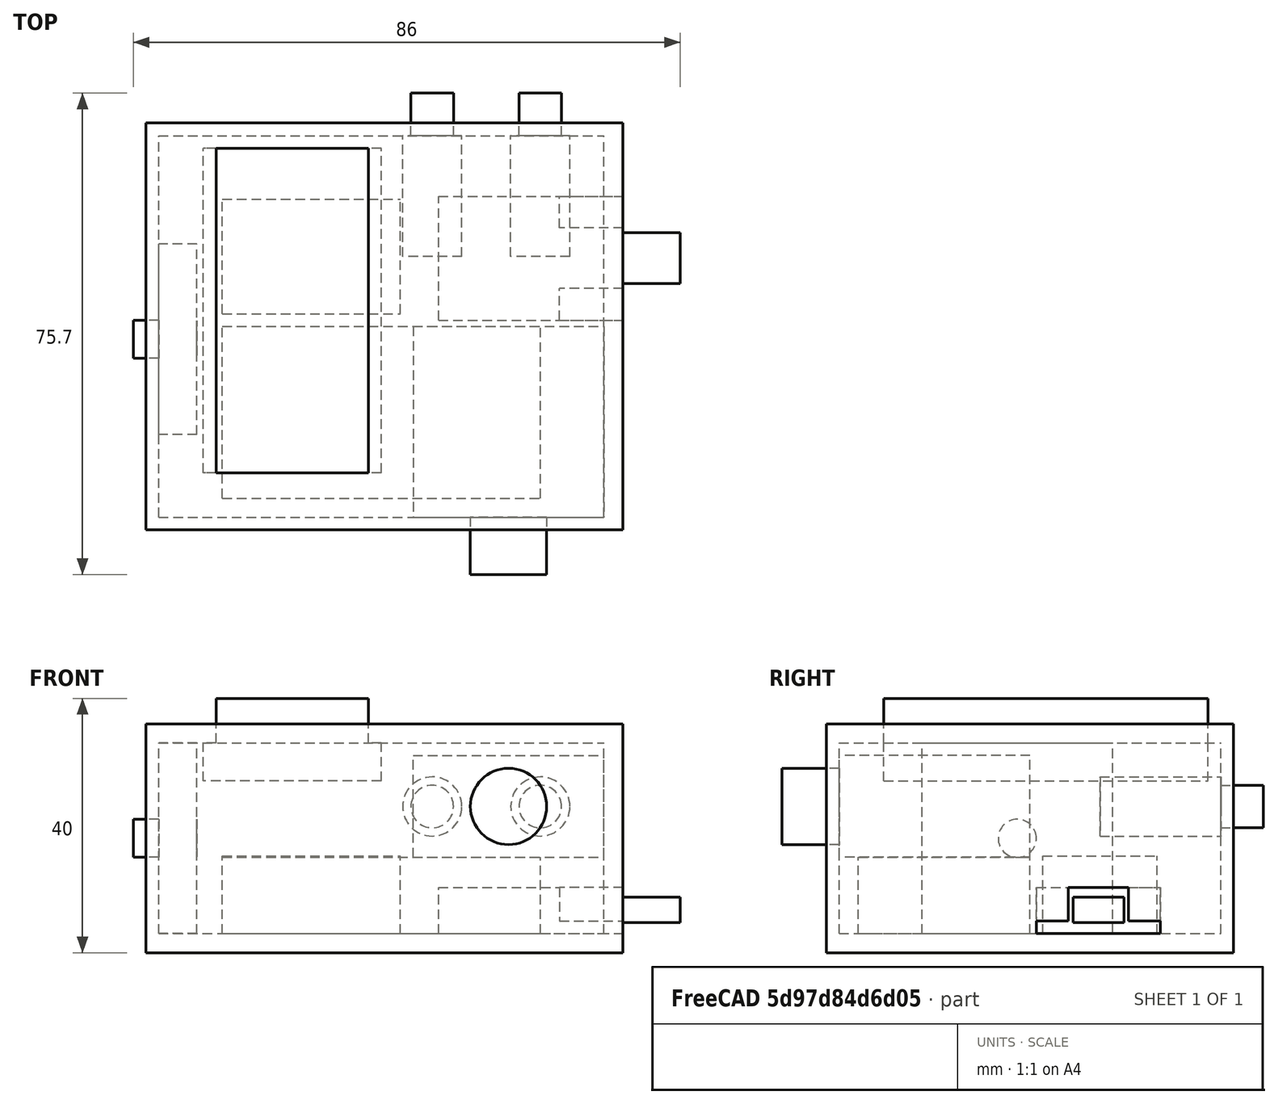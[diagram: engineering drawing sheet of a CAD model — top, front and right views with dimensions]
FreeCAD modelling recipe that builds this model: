
FCSTD DOCUMENT  (FreeCAD 0.19R)
Label: RoundTimer-precuts
License: All rights reserved
LicenseURL: http://en.wikipedia.org/wiki/All_rights_reserved
objects: Part::Box×12, Part::Cylinder×6, Part::MultiFuse×4, Part::Fuse×2, Part::Cut×2
note: 26 computed .brp shape members not serialized (recipe doc carries the construction recipe); baked Part::Feature solids carry a one-line shape summary decoded from their .brp

FEATURE [Part::Box] Box  label="Cube"
  AttacherType = Attacher::AttachEngine3D
  Height = 30
  Length = 30
  Width = 16
FEATURE [Part::Cylinder] Cylinder
  Angle = 360
  AttacherType = Attacher::AttachEngine3D
  Height = 9
  Placement = pos=(15,8,30) rot=(0,0,1;0rad)
  Radius = 6
FEATURE [Part::Fuse] Fusion  label="Awesome switch"
  Base = -> Box
  Placement = pos=(0,17,12) rot=(1,0,0;1.5708rad)
  Tool = -> Cylinder
FEATURE [Part::Box] Box001  label="Cube001"
  AttacherType = Attacher::AttachEngine3D
  Height = 6
  Length = 51
  Width = 28
FEATURE [Part::Box] Box002  label="Cube002"
  AttacherType = Attacher::AttachEngine3D
  Height = 7
  Length = 51
  Placement = pos=(0,2,6) rot=(0,0,1;0rad)
  Width = 24
FEATURE [Part::MultiFuse] Fusion001  label="LCD Display"
  Placement = pos=(-5,-6,24) rot=(0,0,1;1.5708rad)
  Shapes = -> [Box001,Box002]
FEATURE [Part::Box] Box003  label="Lipo Battery"
  AttacherType = Attacher::AttachEngine3D
  Height = 12
  Length = 50
  Placement = pos=(-30,-10,0) rot=(0,0,1;0rad)
  Width = 27
FEATURE [Part::Cylinder] Cylinder001
  Angle = 360
  AttacherType = Attacher::AttachEngine3D
  Height = 19
  Radius = 4.65
FEATURE [Part::Cylinder] Cylinder002
  Angle = 360
  AttacherType = Attacher::AttachEngine3D
  Height = 6.7
  Placement = pos=(0,0,19) rot=(0,0,1;0rad)
  Radius = 3.35
FEATURE [Part::MultiFuse] Fusion002  label="Push Button mode/reset"
  Placement = pos=(20,28,20) rot=(1,0,0;-1.5708rad)
  Shapes = -> [Cylinder001,Cylinder002]
FEATURE [Part::Cylinder] Cylinder003
  Angle = 360
  AttacherType = Attacher::AttachEngine3D
  Height = 19
  Radius = 4.65
FEATURE [Part::Cylinder] Cylinder004
  Angle = 360
  AttacherType = Attacher::AttachEngine3D
  Height = 6.7
  Placement = pos=(0,0,19) rot=(0,0,1;0rad)
  Radius = 3.35
FEATURE [Part::MultiFuse] Fusion003  label="Push Button start/stop"
  Placement = pos=(3,28,20) rot=(1,0,0;-1.5708rad)
  Shapes = -> [Cylinder003,Cylinder004]
FEATURE [Part::Box] Box004  label="Cube003"
  AttacherType = Attacher::AttachEngine3D
  Height = 7.25
  Length = 29
  Width = 19.5
FEATURE [Part::Box] Box005  label="Cube004"
  AttacherType = Attacher::AttachEngine3D
  Height = 4
  Length = 10
  Placement = pos=(28,5.75,1.75) rot=(0,0,1;0rad)
  Width = 8
FEATURE [Part::Box] Box006  label="Cube005"
  AttacherType = Attacher::AttachEngine3D
  Height = 10
  Length = 10
  Placement = pos=(19,-5,2) rot=(0,0,1;0rad)
  Width = 10
FEATURE [Part::MultiFuse] Fusion004
  Shapes = -> [Box004,Box005]
FEATURE [Part::Cut] Cut
  Base = -> Fusion004
  Tool = -> Box006
FEATURE [Part::Box] Box007  label="Cube006"
  AttacherType = Attacher::AttachEngine3D
  Height = 10
  Length = 10
  Placement = pos=(19,14.5,2) rot=(0,0,1;0rad)
  Width = 10
FEATURE [Part::Cut] Cut001  label="USB Battery Charger"
  Base = -> Cut
  Placement = pos=(4,18,0) rot=(0,0,1;0rad)
  Tool = -> Box007
FEATURE [Part::Box] Box008  label="Piezo Driver"
  AttacherType = Attacher::AttachEngine3D
  Height = 12.2
  Length = 28
  Placement = pos=(-30,19,0) rot=(0,0,1;0rad)
  Width = 18
FEATURE [Part::Box] Box009  label="Cube007"
  AttacherType = Attacher::AttachEngine3D
  Height = 6
  Length = 30
  Width = 30
FEATURE [Part::Cylinder] Cylinder005
  Angle = 360
  AttacherType = Attacher::AttachEngine3D
  Height = 10
  Placement = pos=(15,15,0) rot=(0,0,1;0rad)
  Radius = 3
FEATURE [Part::Fuse] Fusion005  label="Piezo Buzzer"
  Base = -> Box009
  Placement = pos=(-34,0,0) rot=(0,1,0;-1.5708rad)
  Tool = -> Cylinder005
FEATURE [Part::Box] Box010  label="OuterBox"
  AttacherType = Attacher::AttachEngine3D
  Height = 36
  Length = 75
  Placement = pos=(-42,-15,-3) rot=(0,0,1;0rad)
  Width = 64
FEATURE [Part::Box] Box011  label="InnerBox"
  AttacherType = Attacher::AttachEngine3D
  Height = 30
  Length = 70
  Placement = pos=(-40,-13,0) rot=(0,0,1;0rad)
  Width = 60
